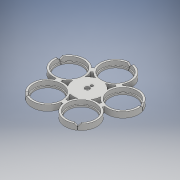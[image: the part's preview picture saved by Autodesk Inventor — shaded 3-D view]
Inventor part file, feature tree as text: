
AUTODESK INVENTOR PART (.ipt)
format: ipt  version: 2017 (Build 210142000, 142)  size: 308,224 bytes
history: native  units: mm
features: extrude x6, sketch x3, chamfer x1
ambient origin geometry x8: Origin, YZ Plane, XZ Plane, XY Plane, X Axis, Y Axis, Z Axis, Center Point
bodies: Solid1 (feature_tree)
feature tree (10):
  sketch  "Sketch1"  dims[d5=50.0mm d6=50.0mm d8=360.0deg]
  extrude  "Extrusion1"  Depth=50.0mm TaperAngle=360.0deg
  sketch  "Sketch2"  dims[d10=3.0mm d11=2.5mm]
  extrude  "Extrusion2"  Depth=3.0mm
  extrude  "Extrusion3"  Depth=24.75mm
  extrude  "Extrusion4"  Depth=3.0mm
  extrude  "Extrusion5"  Depth=3.0mm TaperAngle=0.0deg
  chamfer  "Chamfer1"  Distance=3.0mm
  extrude  "Extrusion6"  Depth=3.0mm
  sketch  "Sketch3"  dims[d12=10.0mm d13=0.0mm d14=24.75mm d15=8.1mm d16=3.0mm d17=0.0mm d18=3.0mm d19=0.0mm d20=9.0mm d21=23.0mm d22=50.0mm d24=360.0deg d26=10.0mm d27=0.0mm d28=8.1mm d29=4.5mm d30=3.0mm d31=0.0mm d32=4.0mm d33=2.0mm d34=45.0deg d35=4.5mm d36=3.0mm d37=0.0mm]
